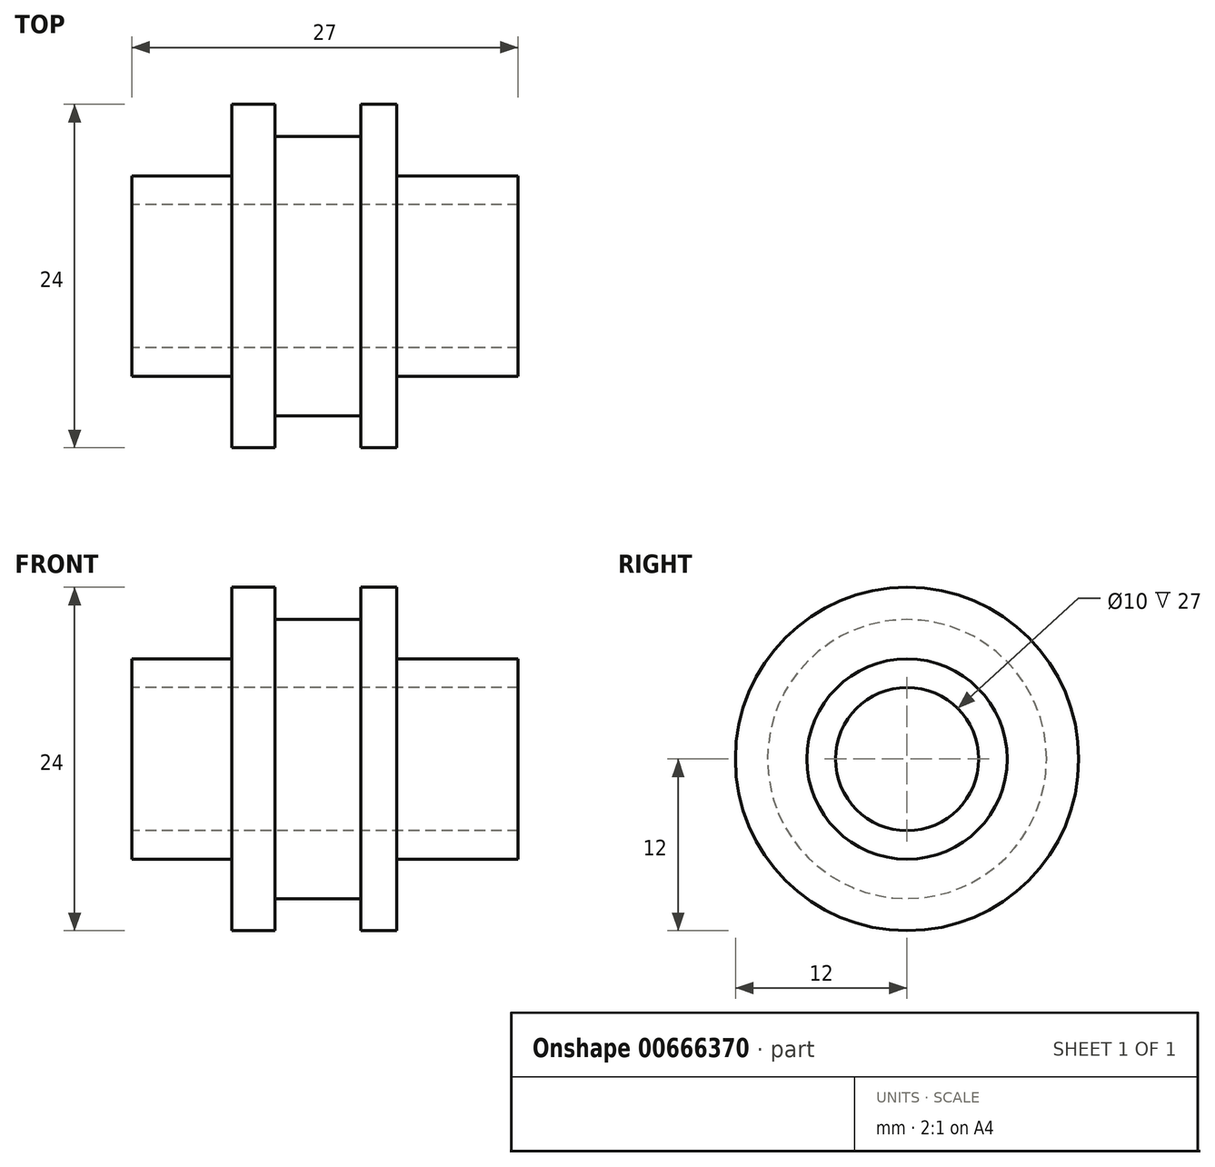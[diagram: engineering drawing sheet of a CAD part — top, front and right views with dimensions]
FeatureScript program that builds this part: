
annotation { "Feature Type Name" : "Feature", "Feature Type Description" : "" }
export const myFeature = defineFeature(function(context is Context, id is Id, definition is map)
    precondition{}
    {
        {
            var Q0;
            Q0=qCreatedBy(makeId("Front.planeOp"),FACE);
            var sketch = newSketch(context, id + "F0", { "sketchPlane" : qUnion([Q0])});
            skLineSegment(sketch, "E0", {"start": v(0, 0) * mm, "end": v(27, 0) * mm});
            skLineSegment(sketch, "E1", {"start": v(27, 5) * mm, "end": v(27, 7) * mm});
            skLineSegment(sketch, "E2", {"start": v(27, 7) * mm, "end": v(18.5, 7) * mm});
            skLineSegment(sketch, "E3", {"start": v(18.5, 7) * mm, "end": v(18.5, 12) * mm});
            skLineSegment(sketch, "E4", {"start": v(18.5, 12) * mm, "end": v(16, 12) * mm});
            skLineSegment(sketch, "E5", {"start": v(16, 12) * mm, "end": v(16, 9.75) * mm});
            skLineSegment(sketch, "E6", {"start": v(16, 9.75) * mm, "end": v(10, 9.75) * mm});
            skLineSegment(sketch, "E7", {"start": v(10, 9.75) * mm, "end": v(10, 12) * mm});
            skLineSegment(sketch, "E8", {"start": v(10, 12) * mm, "end": v(7, 12) * mm});
            skLineSegment(sketch, "E9", {"start": v(7, 12) * mm, "end": v(7, 7) * mm});
            skLineSegment(sketch, "E10", {"start": v(7, 7) * mm, "end": v(0, 7) * mm});
            skLineSegment(sketch, "E11", {"start": v(0, 7) * mm, "end": v(0, 5) * mm});
            skLineSegment(sketch, "E12.0", {"start": v(0, 5) * mm, "end": v(27, 5) * mm});
            skSolve(sketch);
        }
        {
            var Q0;
            Q0=makeQuery(id+"F0.imprint","IMPRINT",FACE,{"disambiguationData":[TD([[makeQuery(id+"F0.imprint","IMPRINT",EDGE,{"derivedFrom":sQuery(id+"F0.wireOp",EDGE,"E1")}),1.0]])]});
            var Q1;
            Q1=sQuery(id+"F0.wireOp",EDGE,"E0");
            revolve(context, id + "F1", {"entities" : qUnion([Q0]), "axis" : qUnion([Q1]), "revolveType" : RevolveType.FULL});
        }
    });
